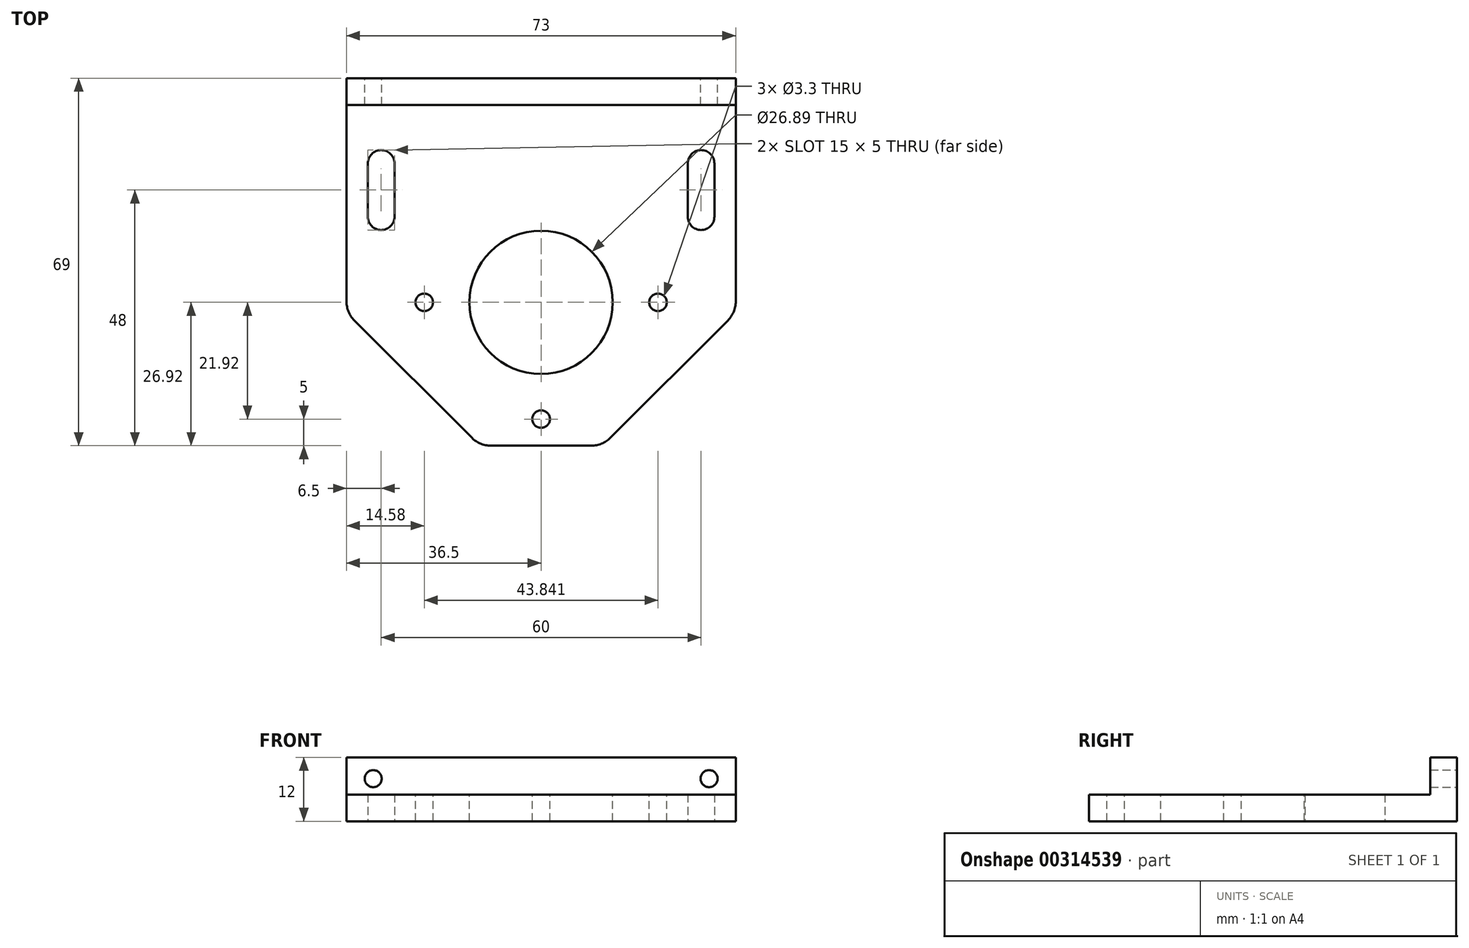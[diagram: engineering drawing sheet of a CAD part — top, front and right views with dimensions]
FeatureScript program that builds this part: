
annotation { "Feature Type Name" : "Feature", "Feature Type Description" : "" }
export const myFeature = defineFeature(function(context is Context, id is Id, definition is map)
    precondition{}
    {
        {
            var Q0;
            Q0=qCreatedBy(makeId("Top.planeOp"),FACE);
            var sketch = newSketch(context, id + "F0", { "sketchPlane" : qUnion([Q0])});
            skLineSegment(sketch, "E0.bottom", {"start": v(-36.5, -29.5) * mm, "end": v(36.5, -29.5) * mm});
            skLineSegment(sketch, "E0.top", {"start": v(-36.5, 29.5) * mm, "end": v(36.5, 29.5) * mm});
            skLineSegment(sketch, "E0.left", {"start": v(-36.5, -29.5) * mm, "end": v(-36.5, 29.5) * mm});
            skLineSegment(sketch, "E0.right", {"start": v(36.5, -29.5) * mm, "end": v(36.5, 29.5) * mm});
            skPoint(sketch, "E0.middle", {"position": v(0, 0) * mm});
            skLineSegment(sketch, "E1", {"start": v(-30, 23.5) * mm, "end": v(-30, 13.5) * mm});
            skLineSegment(sketch, "E2.1.0.0", {"start": v(30, 23.5) * mm, "end": v(30, 13.5) * mm});
            skLineSegment(sketch, "E2.direction1", {"start": v(-30, 13.5) * mm, "end": v(30, 13.5) * mm, "construction": true});
            skArc(sketch, "E3.0.startCap", {"start": v(-32.5, 23.5) * mm, "mid": v(-30, 26) * mm, "end": v(-27.5, 23.5) * mm});
            skArc(sketch, "E3.0.endCap", {"start": v(-27.5, 13.5) * mm, "mid": v(-30, 11) * mm, "end": v(-32.5, 13.5) * mm});
            skLineSegment(sketch, "E3.0.left", {"start": v(-27.5, 23.5) * mm, "end": v(-27.5, 13.5) * mm});
            skLineSegment(sketch, "E3.0.right", {"start": v(-32.5, 23.5) * mm, "end": v(-32.5, 13.5) * mm});
            skArc(sketch, "E3.1.startCap", {"start": v(27.5, 23.5) * mm, "mid": v(30, 26) * mm, "end": v(32.5, 23.5) * mm});
            skArc(sketch, "E3.1.endCap", {"start": v(32.5, 13.5) * mm, "mid": v(30, 11) * mm, "end": v(27.5, 13.5) * mm});
            skLineSegment(sketch, "E3.1.left", {"start": v(32.5, 23.5) * mm, "end": v(32.5, 13.5) * mm});
            skLineSegment(sketch, "E3.1.right", {"start": v(27.5, 23.5) * mm, "end": v(27.5, 13.5) * mm});
            skSolve(sketch);
        }
        {
            var Q0;
            Q0=qSketchRegion(id+"F0",true);
            extrude(context, id + "F1", {"entities" : qUnion([Q0]), "depth" : 5 * mm});
        }
        {
            var Q0;
            Q0=makeQuery(id+"F1.opExtrude","SWEPT_EDGE",EDGE,{"disambiguationData":[OSD([sQuery(id+"F0.wireOp",EDGE,"E0.bottom"),sQuery(id+"F0.wireOp",EDGE,"E0.left")])]});
            var Q1;
            Q1=makeQuery(id+"F1.opExtrude","SWEPT_EDGE",EDGE,{"disambiguationData":[OSD([sQuery(id+"F0.wireOp",EDGE,"E0.bottom"),sQuery(id+"F0.wireOp",EDGE,"E0.right")])]});
            chamfer(context, id + "F2", {"entities" : qUnion([Q0, Q1]), "width" : 25 * mm, "tangentPropagation" : true});
        }
        {
            var Q0;
            Q0=makeQuery(id+"F1.opExtrude","CAP_FACE",FACE,{"disambiguationData":[OSD([sQuery(id+"F0.wireOp",EDGE,"E0.bottom"),sQuery(id+"F0.wireOp",EDGE,"E0.top"),sQuery(id+"F0.wireOp",EDGE,"E0.left"),sQuery(id+"F0.wireOp",EDGE,"E0.right"),sQuery(id+"F0.wireOp",EDGE,"E3.0.startCap"),sQuery(id+"F0.wireOp",EDGE,"E3.0.endCap"),sQuery(id+"F0.wireOp",EDGE,"E3.0.left"),sQuery(id+"F0.wireOp",EDGE,"E3.0.right"),sQuery(id+"F0.wireOp",EDGE,"E3.1.startCap"),sQuery(id+"F0.wireOp",EDGE,"E3.1.endCap"),sQuery(id+"F0.wireOp",EDGE,"E3.1.left"),sQuery(id+"F0.wireOp",EDGE,"E3.1.right")])],"isStart":false});
            var sketch = newSketch(context, id + "F3", { "sketchPlane" : qUnion([Q0])});
            skPoint(sketch, "E4", {"position": v(0, -24.5) * mm});
            skLineSegment(sketch, "E5", {"start": v(0, -24.5) * mm, "end": v(-21.92, -2.58) * mm, "construction": true});
            skLineSegment(sketch, "E6", {"start": v(0, -24.5) * mm, "end": v(-61.13, -24.5) * mm, "construction": true});
            skLineSegment(sketch, "E7.MirrorCS", {"start": v(0, -24.5) * mm, "end": v(21.92, -2.58) * mm, "construction": true});
            skPoint(sketch, "E8", {"position": v(-21.92, -2.58) * mm});
            skPoint(sketch, "E9", {"position": v(21.92, -2.58) * mm});
            skCircle(sketch, "E10", {"center": v(0, -2.58) * mm, "radius": 13.45 * mm});
            skSolve(sketch);
        }
        {
            var Q0;
            Q0=sQuery(id+"F3.wireOp",VERTEX,"E8");
            var Q1;
            Q1=sQuery(id+"F3.wireOp",VERTEX,"E4");
            var Q2;
            Q2=sQuery(id+"F3.wireOp",VERTEX,"E9");
            var Q3;
            Q3=makeQuery(id+"F1.opExtrude","SWEPT_BODY",BODY,{"disambiguationData":[OSD([sQuery(id+"F0.wireOp",EDGE,"E0.bottom"),sQuery(id+"F0.wireOp",EDGE,"E0.top"),sQuery(id+"F0.wireOp",EDGE,"E0.left"),sQuery(id+"F0.wireOp",EDGE,"E0.right"),sQuery(id+"F0.wireOp",EDGE,"E3.0.startCap"),sQuery(id+"F0.wireOp",EDGE,"E3.0.endCap"),sQuery(id+"F0.wireOp",EDGE,"E3.0.left"),sQuery(id+"F0.wireOp",EDGE,"E3.0.right"),sQuery(id+"F0.wireOp",EDGE,"E3.1.startCap"),sQuery(id+"F0.wireOp",EDGE,"E3.1.endCap"),sQuery(id+"F0.wireOp",EDGE,"E3.1.left"),sQuery(id+"F0.wireOp",EDGE,"E3.1.right")])]});
            hole(context, id + "F4", {"style" : HoleStyle.SIMPLE, "endStyle" : HoleEndStyle.BLIND, "standardTappedOrClearance" : lookupTablePath({ "standard" : "ISO", "fit" : "Normal", "size" : "M3", "type" : "Clearance" }), "standardBlindInLast" : lookupTablePath({ "fit" : "Standard", "standard" : "ISO", "size" : "M3", "type" : "Clearance" }), "holeDiameter" : 3.3 * mm, "holeDepth" : 13.8 * mm, "tappedDepth" : 12 * mm, "tapClearance" : 3, "locations" : qUnion([Q0, Q1, Q2]), "scope" : qUnion([Q3])});
        }
        {
            var Q0;
            Q0=qSketchRegion(id+"F3",true);
            extrude(context, id + "F5", {"entities" : qUnion([Q0]), "operationType" : NewBodyOperationType.REMOVE, "endBound" : BoundingType.UP_TO_NEXT, "oppositeDirection" : true, "depth" : 25 * mm});
        }
        {
            var Q0;
            Q0=makeQuery(id+"F1.opExtrude","SWEPT_FACE",FACE,{"disambiguationData":[OSD([sQuery(id+"F0.wireOp",EDGE,"E0.top")])]});
            var sketch = newSketch(context, id + "F6", { "sketchPlane" : qUnion([Q0])});
            skLineSegment(sketch, "E11.bottom", {"start": v(-36.5, 5) * mm, "end": v(36.5, 5) * mm});
            skLineSegment(sketch, "E11.top", {"start": v(-36.5, 0) * mm, "end": v(36.5, 0) * mm});
            skLineSegment(sketch, "E11.left", {"start": v(-36.5, 5) * mm, "end": v(-36.5, 0) * mm});
            skLineSegment(sketch, "E11.right", {"start": v(36.5, 5) * mm, "end": v(36.5, 0) * mm});
            skSolve(sketch);
        }
        {
            var Q0;
            Q0 = qSketchRegion(id + "F6", true);
            extrude(context, id + "F7", {"entities" : qUnion([Q0]), "operationType" : NewBodyOperationType.ADD, "depth" : 5 * mm});
        }
        {
            var Q0;
            Q0=makeQuery(id+"F7.opExtrude","CAP_FACE",FACE,{"disambiguationData":[OSD([sQuery(id+"F6.wireOp",EDGE,"E11.bottom"),sQuery(id+"F6.wireOp",EDGE,"E11.top"),sQuery(id+"F6.wireOp",EDGE,"E11.left"),sQuery(id+"F6.wireOp",EDGE,"E11.right")])],"isStart":false});
            var sketch = newSketch(context, id + "F8", { "sketchPlane" : qUnion([Q0])});
            skLineSegment(sketch, "E12.bottom", {"start": v(-36.5, 0) * mm, "end": v(36.5, 0) * mm});
            skLineSegment(sketch, "E12.top", {"start": v(-36.5, 12) * mm, "end": v(36.5, 12) * mm});
            skLineSegment(sketch, "E12.left", {"start": v(-36.5, 0) * mm, "end": v(-36.5, 12) * mm});
            skLineSegment(sketch, "E12.right", {"start": v(36.5, 0) * mm, "end": v(36.5, 12) * mm});
            skSolve(sketch);
        }
        {
            var Q0;
            Q0 = qSketchRegion(id + "F8", true);
            extrude(context, id + "F9", {"entities" : qUnion([Q0]), "operationType" : NewBodyOperationType.ADD, "depth" : 5 * mm});
        }
        {
            var Q0;
            Q0=makeQuery(id+"F9.opExtrude","CAP_FACE",FACE,{"disambiguationData":[OSD([sQuery(id+"F8.wireOp",EDGE,"E12.bottom"),sQuery(id+"F8.wireOp",EDGE,"E12.top"),sQuery(id+"F8.wireOp",EDGE,"E12.left"),sQuery(id+"F8.wireOp",EDGE,"E12.right")])],"isStart":false});
            var sketch = newSketch(context, id + "F10", { "sketchPlane" : qUnion([Q0])});
            skPoint(sketch, "E13", {"position": v(-31.5, 8) * mm});
            skPoint(sketch, "E14.MirrorP", {"position": v(31.5, 8) * mm});
            skSolve(sketch);
        }
        {
            var Q0;
            Q0=sQuery(id+"F10.wireOp",VERTEX,"E13");
            var Q1;
            Q1=sQuery(id+"F10.wireOp",VERTEX,"E14.MirrorP");
            var Q2;
            Q2=makeQuery(id+"F1.opExtrude","SWEPT_BODY",BODY,{"disambiguationData":[OSD([sQuery(id+"F0.wireOp",EDGE,"E0.bottom"),sQuery(id+"F0.wireOp",EDGE,"E0.top"),sQuery(id+"F0.wireOp",EDGE,"E0.left"),sQuery(id+"F0.wireOp",EDGE,"E0.right"),sQuery(id+"F0.wireOp",EDGE,"E3.0.startCap"),sQuery(id+"F0.wireOp",EDGE,"E3.0.endCap"),sQuery(id+"F0.wireOp",EDGE,"E3.0.left"),sQuery(id+"F0.wireOp",EDGE,"E3.0.right"),sQuery(id+"F0.wireOp",EDGE,"E3.1.startCap"),sQuery(id+"F0.wireOp",EDGE,"E3.1.endCap"),sQuery(id+"F0.wireOp",EDGE,"E3.1.left"),sQuery(id+"F0.wireOp",EDGE,"E3.1.right")])]});
            hole(context, id + "F11", {"style" : HoleStyle.SIMPLE, "endStyle" : HoleEndStyle.THROUGH, "standardTappedOrClearance" : lookupTablePath({ "standard" : "ISO", "engagement" : "75%", "pitch" : "0.75 mm", "size" : "M4", "type" : "Tapped" }), "standardBlindInLast" : lookupTablePath({ "standard" : "ISO", "engagement" : "75%", "pitch" : "0.75 mm", "size" : "M4", "type" : "Tapped" }), "holeDiameter" : 3.2 * mm, "showTappedDepth" : true, "isTappedThrough" : true, "tappedDepth" : 12 * mm, "tapClearance" : 3, "locations" : qUnion([Q0, Q1]), "scope" : qUnion([Q2])});
        }
        {
            var Q0;
            {var subQ0=sQuery(id+"F0.wireOp",EDGE,"E0.right");Q0=makeQuery(id+"F2.opChamfer","BLEND_EDGE",EDGE,{"blendedFrom":[makeQuery(id+"F1.opExtrude","SWEPT_EDGE",EDGE,{"disambiguationData":[OSD([sQuery(id+"F0.wireOp",EDGE,"E0.bottom"),subQ0])]}),makeQuery(id+"F1.opExtrude","SWEPT_FACE",FACE,{"disambiguationData":[OSD([subQ0])]})],"blendedInto":[makeQuery(id+"F1.opExtrude","SWEPT_FACE",FACE,{"disambiguationData":[OSD([subQ0])]})]});}
            var Q1;
            {var subQ0=sQuery(id+"F0.wireOp",EDGE,"E0.bottom");Q1=makeQuery(id+"F2.opChamfer","BLEND_EDGE",EDGE,{"blendedFrom":[makeQuery(id+"F1.opExtrude","SWEPT_EDGE",EDGE,{"disambiguationData":[OSD([subQ0,sQuery(id+"F0.wireOp",EDGE,"E0.right")])]}),makeQuery(id+"F1.opExtrude","SWEPT_FACE",FACE,{"disambiguationData":[OSD([subQ0])]})],"blendedInto":[makeQuery(id+"F1.opExtrude","SWEPT_FACE",FACE,{"disambiguationData":[OSD([subQ0])]})]});}
            var Q2;
            {var subQ0=sQuery(id+"F0.wireOp",EDGE,"E0.bottom");Q2=makeQuery(id+"F2.opChamfer","BLEND_EDGE",EDGE,{"blendedFrom":[makeQuery(id+"F1.opExtrude","SWEPT_EDGE",EDGE,{"disambiguationData":[OSD([subQ0,sQuery(id+"F0.wireOp",EDGE,"E0.left")])]}),makeQuery(id+"F1.opExtrude","SWEPT_FACE",FACE,{"disambiguationData":[OSD([subQ0])]})],"blendedInto":[makeQuery(id+"F1.opExtrude","SWEPT_FACE",FACE,{"disambiguationData":[OSD([subQ0])]})]});}
            var Q3;
            {var subQ0=sQuery(id+"F0.wireOp",EDGE,"E0.left");Q3=makeQuery(id+"F2.opChamfer","BLEND_EDGE",EDGE,{"blendedFrom":[makeQuery(id+"F1.opExtrude","SWEPT_EDGE",EDGE,{"disambiguationData":[OSD([sQuery(id+"F0.wireOp",EDGE,"E0.bottom"),subQ0])]}),makeQuery(id+"F1.opExtrude","SWEPT_FACE",FACE,{"disambiguationData":[OSD([subQ0])]})],"blendedInto":[makeQuery(id+"F1.opExtrude","SWEPT_FACE",FACE,{"disambiguationData":[OSD([subQ0])]})]});}
            fillet(context, id + "F12", {"entities" : qUnion([Q0, Q1, Q2, Q3]), "radius" : 5 * mm, "tangentPropagation" : true, "allowEdgeOverflow" : false});
        }
    });
